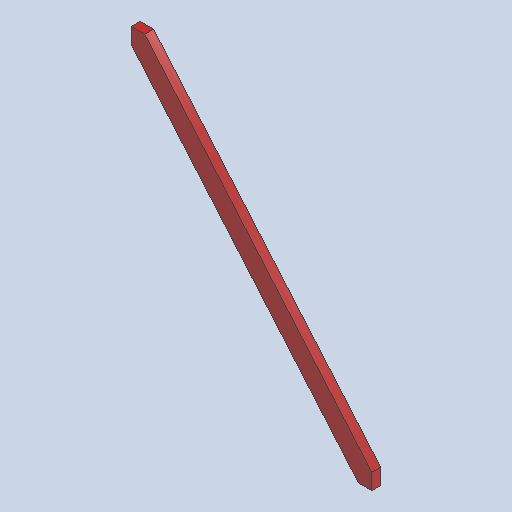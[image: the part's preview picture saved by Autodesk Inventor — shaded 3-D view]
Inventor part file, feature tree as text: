
AUTODESK INVENTOR PART (.ipt)
format: ipt  version: 2025 (Build 290162000, 162)  size: 92,160 bytes
history: native  units: in
note: dims shown in document units (in); Inventor stores cm internally (conversion verified against a paired STEP export)
features: other x7, reference x4, extrude x1, sketch x1
ambient origin geometry x8: Origin, YZ Plane, XZ Plane, XY Plane, X Axis, Y Axis, Z Axis, Center Point
bodies: Solid1 (feature_tree)
feature tree (13):
  extrude  "Extrusion1"  [1 undecoded]
  sketch  "Sketch1"  dims[d2=1.5in d3=0.0in]
  reference  "Reference1"
  reference  "Reference2"
  reference  "Reference3"
  reference  "Reference4"
  other  "<userpath>\Documents\USCTigerBurn24\Tburn24\Legs0\B_Legs0.iam"
  other  "B_Legs0.iam"
  other  "4x2x4:1"
  other  "3'5x2x4:1"
  other  "4x2x4:2"
  other  "3'5x2x4:4"
  other  "Finish1"
note: 1 required parameter value undecoded (feature->parameter linkage not recoverable at this tier; creation-order binding heuristic only, values carry confidence <= 0.55)
